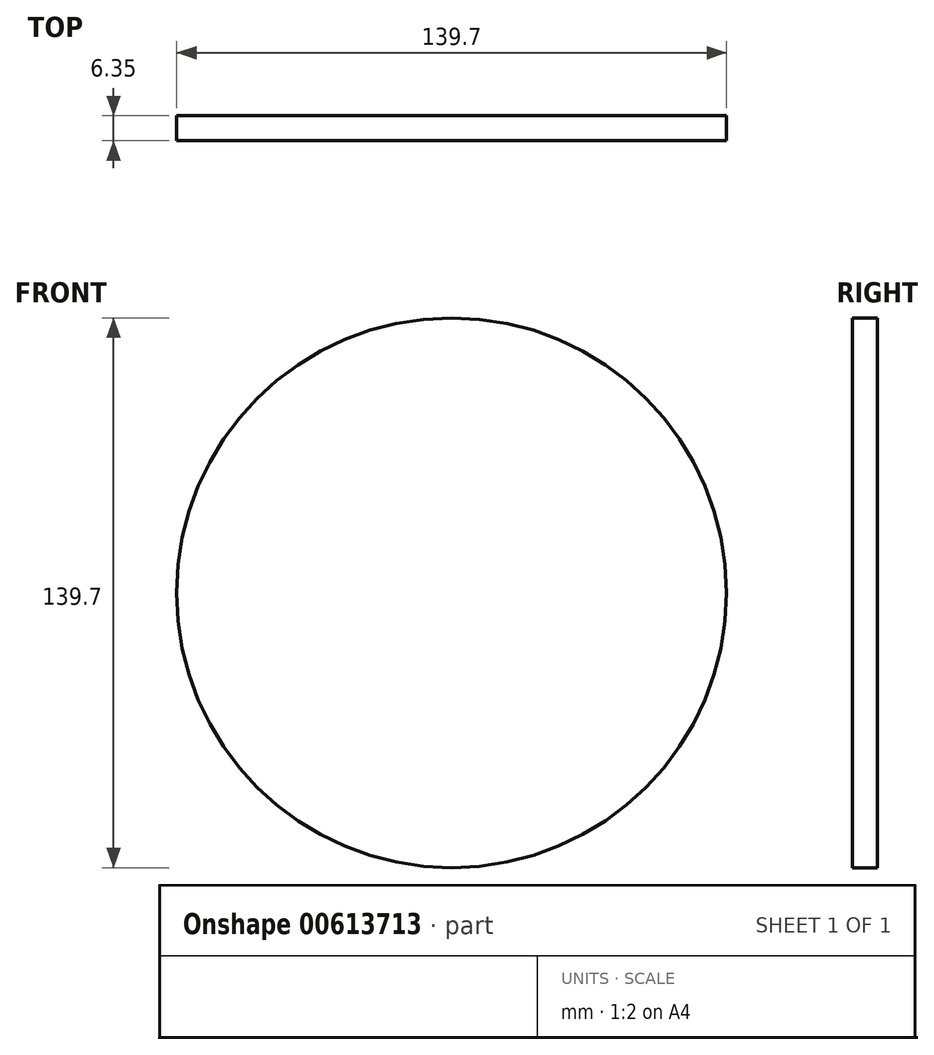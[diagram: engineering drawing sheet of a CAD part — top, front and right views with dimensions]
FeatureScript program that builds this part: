
annotation { "Feature Type Name" : "Feature", "Feature Type Description" : "" }
export const myFeature = defineFeature(function(context is Context, id is Id, definition is map)
    precondition{}
    {
        {
            var Q0;
            Q0=qCreatedBy(makeId("Front.planeOp"),FACE);
            var sketch = newSketch(context, id + "F0", { "sketchPlane" : qUnion([Q0])});
            skLineSegment(sketch, "E0.bottom", {"start": v(-63.5, 76.2) * mm, "end": v(63.5, 76.2) * mm});
            skLineSegment(sketch, "E0.top", {"start": v(-63.5, -76.2) * mm, "end": v(63.5, -76.2) * mm});
            skLineSegment(sketch, "E0.left", {"start": v(-76.2, 63.5) * mm, "end": v(-76.2, -63.5) * mm});
            skLineSegment(sketch, "E0.right", {"start": v(76.2, 63.5) * mm, "end": v(76.2, -63.5) * mm});
            skPoint(sketch, "E1.visualSharp", {"position": v(-76.2, 76.2) * mm});
            skArc(sketch, "E1.filletArc", {"start": v(-63.5, 76.2) * mm, "mid": v(-72.48, 72.48) * mm, "end": v(-76.2, 63.5) * mm});
            skPoint(sketch, "E2.visualSharp", {"position": v(-76.2, -76.2) * mm});
            skArc(sketch, "E2.filletArc", {"start": v(-76.2, -63.5) * mm, "mid": v(-72.48, -72.48) * mm, "end": v(-63.5, -76.2) * mm});
            skPoint(sketch, "E3.visualSharp", {"position": v(76.2, 76.2) * mm});
            skArc(sketch, "E3.filletArc", {"start": v(76.2, 63.5) * mm, "mid": v(72.48, 72.48) * mm, "end": v(63.5, 76.2) * mm});
            skPoint(sketch, "E4.visualSharp", {"position": v(76.2, -76.2) * mm});
            skArc(sketch, "E4.filletArc", {"start": v(63.5, -76.2) * mm, "mid": v(72.48, -72.48) * mm, "end": v(76.2, -63.5) * mm});
            skLineSegment(sketch, "E5.bottom", {"start": v(-57.15, 69.85) * mm, "end": v(57.15, 69.85) * mm});
            skLineSegment(sketch, "E5.top", {"start": v(-57.15, -69.85) * mm, "end": v(57.15, -69.85) * mm});
            skLineSegment(sketch, "E5.left", {"start": v(-69.85, 57.15) * mm, "end": v(-69.85, -57.15) * mm});
            skLineSegment(sketch, "E5.right", {"start": v(69.85, 57.15) * mm, "end": v(69.85, -57.15) * mm});
            skPoint(sketch, "E6.visualSharp", {"position": v(-69.85, 69.85) * mm});
            skArc(sketch, "E6.filletArc", {"start": v(-57.15, 69.85) * mm, "mid": v(-66.13, 66.13) * mm, "end": v(-69.85, 57.15) * mm});
            skPoint(sketch, "E7.visualSharp", {"position": v(-69.85, -69.85) * mm});
            skArc(sketch, "E7.filletArc", {"start": v(-69.85, -57.15) * mm, "mid": v(-66.13, -66.13) * mm, "end": v(-57.15, -69.85) * mm});
            skPoint(sketch, "E8.visualSharp", {"position": v(69.85, 69.85) * mm});
            skArc(sketch, "E8.filletArc", {"start": v(69.85, 57.15) * mm, "mid": v(66.13, 66.13) * mm, "end": v(57.15, 69.85) * mm});
            skPoint(sketch, "E9.visualSharp", {"position": v(69.85, -69.85) * mm});
            skArc(sketch, "E9.filletArc", {"start": v(57.15, -69.85) * mm, "mid": v(66.13, -66.13) * mm, "end": v(69.85, -57.15) * mm});
            skCircle(sketch, "E10", {"center": v(0, 0) * mm, "radius": 69.85 * mm});
            skSolve(sketch);
        }
        {
            var Q0;
            {var subQ0=sQuery(id+"F0.wireOp",EDGE,"E10");var subQ1=makeQuery(id+"F0.imprint","INTERSECT",VERTEX,{"derivedFrom":[sQuery(id+"F0.wireOp",EDGE,"E5.bottom"),subQ0]});Q0=makeQuery(id+"F0.imprint","IMPRINT",FACE,{"disambiguationData":[TD([[makeQuery(id+"F0.imprint","IMPRINT",EDGE,{"disambiguationData":[TD([[subQ1,1.0]])],"derivedFrom":subQ0}),1.0]])]});}
            extrude(context, id + "F1", {"entities" : qUnion([Q0]), "oppositeDirection" : true, "depth" : 6.35 * mm, "offsetDistance" : 25.4 * mm});
        }
    });
